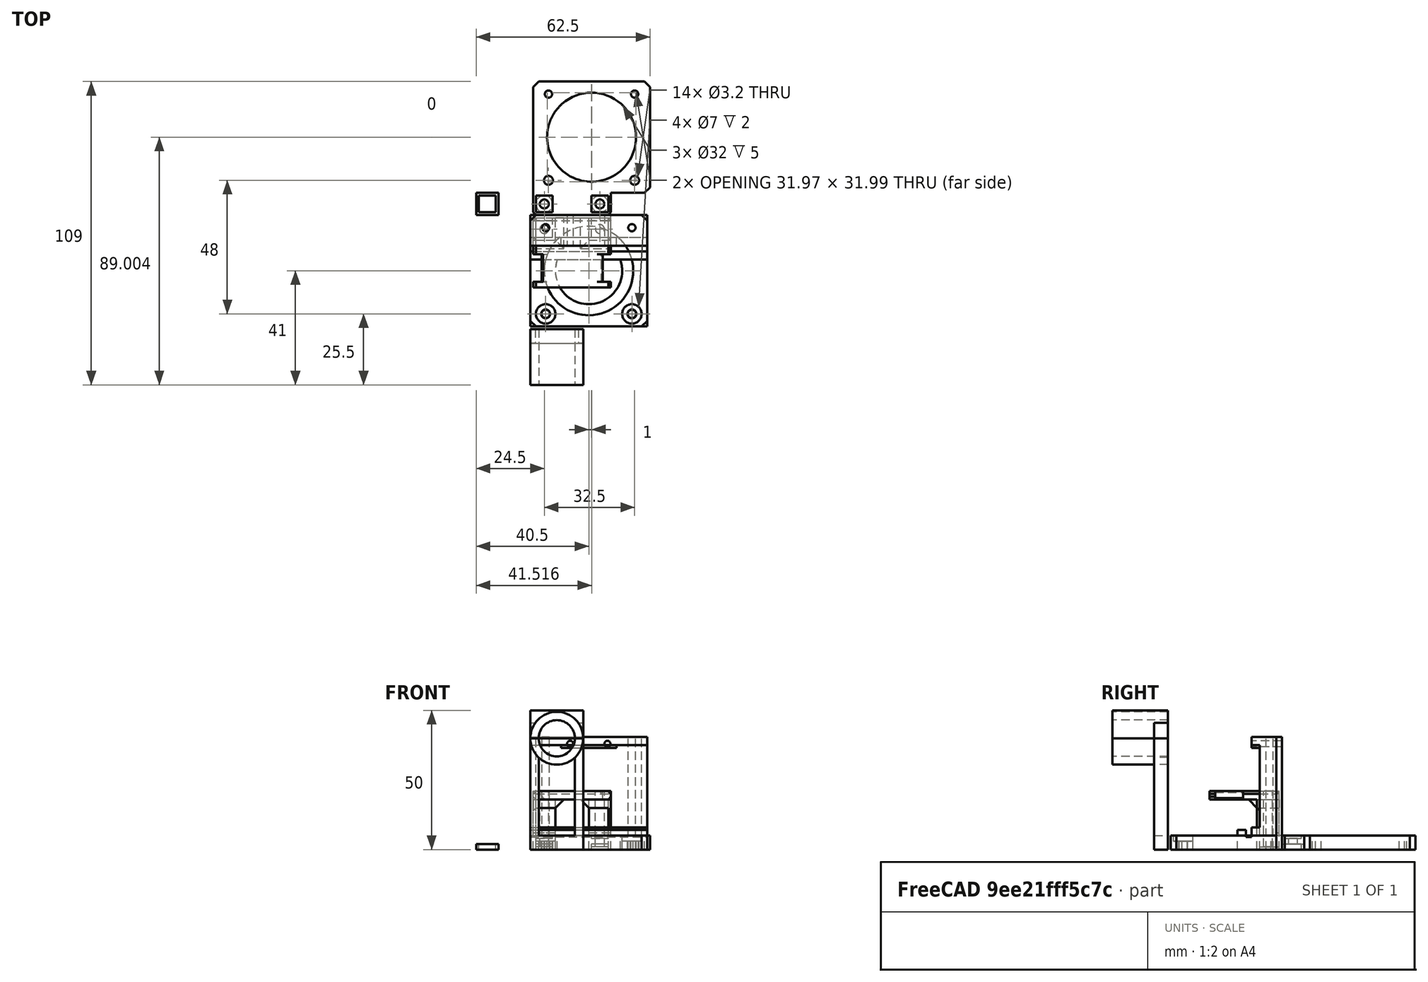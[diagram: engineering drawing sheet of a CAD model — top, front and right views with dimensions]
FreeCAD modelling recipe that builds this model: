
FCSTD DOCUMENT  (FreeCAD 0.18R14555 (Git shallow))
Label: extruder-wirebox-bottom
License: All rights reserved
LicenseURL: http://en.wikipedia.org/wiki/All_rights_reserved
objects: Part::Box×41, Part::Cylinder×25, Part::MultiFuse×21, Part::Cut×20, Part::Chamfer×9, Part::Feature×5, App::DocumentObjectGroup×1, Part::MultiCommon×1, Part::Fillet×1
note: 123 computed .brp shape members not serialized (recipe doc carries the construction recipe); baked Part::Feature solids carry a one-line shape summary decoded from their .brp

FEATURE [Part::Box] Box  label="Cube"
  AttacherType = Attacher::AttachEngine3D
  Height = 5
  Length = 42
  Placement = pos=(-1,-40,0) rot=(0,0,1;0rad)
  Width = 40
FEATURE [Part::Cylinder] Cylinder
  Angle = 360
  AttacherType = Attacher::AttachEngine3D
  Height = 50
  Placement = pos=(4.5,-4.5,0) rot=(0,0,1;0rad)
  Radius = 1.3
FEATURE [Part::Cylinder] Cylinder001
  Angle = 360
  AttacherType = Attacher::AttachEngine3D
  Height = 50
  Placement = pos=(35.5,-4.5,0) rot=(0,0,1;0rad)
  Radius = 1.3
FEATURE [Part::Box] Box001  label="Cube001"
  AttacherType = Attacher::AttachEngine3D
  Height = 40.5
  Length = 42
  Placement = pos=(-1,-8,0) rot=(0,0,1;0rad)
  Width = 8
FEATURE [Part::Box] Box002  label="Cube002"
  AttacherType = Attacher::AttachEngine3D
  Height = 8
  Length = 42
  Placement = pos=(-1,-11,0) rot=(0,0,1;0rad)
  Width = 3
FEATURE [Part::Box] Box003  label="Cube003"
  AttacherType = Attacher::AttachEngine3D
  Height = 7
  Length = 42
  Placement = pos=(-1,-16,0) rot=(0,0,1;0rad)
  Width = 3
FEATURE [Part::Cylinder] Cylinder006
  Angle = 360
  AttacherType = Attacher::AttachEngine3D
  Height = 5
  Placement = pos=(20,-20,0) rot=(0,0,1;0rad)
  Radius = 12
FEATURE [Part::Box] Box004  label="Cube004"
  AttacherType = Attacher::AttachEngine3D
  Height = 5
  Length = 42
  Placement = pos=(-1,-16,0) rot=(0,0,1;0rad)
  Width = 16
FEATURE [Part::Cut] Cut
  Base = -> Cylinder006
  Tool = -> Box004
FEATURE [Part::Box] Box005  label="Cube005"
  AttacherType = Attacher::AttachEngine3D
  Height = 5
  Length = 42
  Placement = pos=(-1,-11,35.5) rot=(0,0,1;0rad)
  Width = 3
FEATURE [Part::Cylinder] Cylinder007
  Angle = 360
  AttacherType = Attacher::AttachEngine3D
  Height = 11
  Placement = pos=(13.3,8e-15,38) rot=(1,0,0;1.5708rad)
  Radius = 1.1
FEATURE [Part::Cylinder] Cylinder008
  Angle = 360
  AttacherType = Attacher::AttachEngine3D
  Height = 11
  Placement = pos=(26.7,8e-15,38) rot=(1,0,0;1.5708rad)
  Radius = 1.1
FEATURE [App::DocumentObjectGroup] Group
FEATURE [Part::MultiFuse] Fusion
  Shapes = -> [Box005,Box001,Box003,Box002,Box]
FEATURE [Part::Box] Box006  label="Cube006"
  AttacherType = Attacher::AttachEngine3D
  Height = 2
  Length = 11
  Placement = pos=(-1,-11,35.5) rot=(0,0,1;0rad)
  Width = 3
FEATURE [Part::Box] Box007  label="Cube007"
  AttacherType = Attacher::AttachEngine3D
  Height = 2
  Length = 11
  Placement = pos=(30,-11,35.5) rot=(0,0,1;0rad)
  Width = 3
FEATURE [Part::Box] Box008  label="Cube008"
  AttacherType = Attacher::AttachEngine3D
  Height = 1
  Length = 20
  Placement = pos=(10,-11,35.5) rot=(0,0,1;0rad)
  Width = 3
FEATURE [Part::Box] Box009  label="Cube009"
  AttacherType = Attacher::AttachEngine3D
  Height = 2
  Length = 42
  Placement = pos=(-1,-13,4.5) rot=(0,0,1;0rad)
  Width = 2
FEATURE [Part::MultiFuse] Fusion002
  Shapes = -> [Box009,Box008,Box007,Box006]
FEATURE [Part::Cylinder] Cylinder009
  Angle = 360
  AttacherType = Attacher::AttachEngine3D
  Height = 2
  Placement = pos=(4.5,-35.5,3) rot=(0,0,1;0rad)
  Radius = 3.5
FEATURE [Part::Cylinder] Cylinder010
  Angle = 360
  AttacherType = Attacher::AttachEngine3D
  Height = 2
  Placement = pos=(35.5,-35.5,3) rot=(0,0,1;0rad)
  Radius = 3.5
FEATURE [Part::Cylinder] Cylinder011
  Angle = 360
  AttacherType = Attacher::AttachEngine3D
  Height = 5
  Placement = pos=(35.5,-35.5,0) rot=(0,0,1;0rad)
  Radius = 1.5
FEATURE [Part::Cylinder] Cylinder012
  Angle = 360
  AttacherType = Attacher::AttachEngine3D
  Height = 5
  Placement = pos=(4.5,-35.5,0) rot=(0,0,1;0rad)
  Radius = 1.5
FEATURE [Part::Cut] Cut001
  Base = -> Fusion
  Tool = -> Cut
FEATURE [Part::MultiFuse] Fusion003
  Shapes = -> [Cylinder,Cylinder001,Cylinder007,Cylinder008,Cylinder009,Cylinder010,Cylinder011,Cylinder012]
FEATURE [Part::Cut] Cut002
  Base = -> Cut001
  Tool = -> Fusion002
FEATURE [Part::Cut] Cut003
  Base = -> Cut002
  Tool = -> Fusion003
FEATURE [Part::Feature] Cut003001  label="Cut004"
  shape: bbox 42 x 40 x 40.5 mm, 31 faces (baked)
FEATURE [Part::Chamfer] Chamfer
  Base = -> Cut003001
  Edges = 4 edges r=2: [Edge27,Edge29,Edge47,Edge80]
FEATURE [Part::Feature] Chamfer_solid  label="Chamfer (Solid)"
  shape: bbox 42 x 40 x 40.5 mm, 35 faces (baked)
FEATURE [Part::Box] Box010  label="Cube010"
  AttacherType = Attacher::AttachEngine3D
  Height = 3
  Length = 11
  Placement = pos=(30,-11,37.5) rot=(0,0,1;0rad)
  Width = 3
FEATURE [Part::Box] Box011  label="Cube011"
  AttacherType = Attacher::AttachEngine3D
  Height = 3
  Length = 11
  Placement = pos=(-1,-11,37.5) rot=(0,0,1;0rad)
  Width = 3
FEATURE [Part::Box] Box012  label="Cube012"
  AttacherType = Attacher::AttachEngine3D
  Height = 1
  Length = 20
  Placement = pos=(10,-11,36.5) rot=(0,0,1;0rad)
  Width = 3
FEATURE [Part::Cylinder] Cylinder013
  Angle = 360
  AttacherType = Attacher::AttachEngine3D
  Height = 3
  Placement = pos=(4.5,-35.5,0) rot=(0,0,1;0rad)
  Radius = 1.6
FEATURE [Part::Cylinder] Cylinder014
  Angle = 360
  AttacherType = Attacher::AttachEngine3D
  Height = 3
  Placement = pos=(35.5,-35.5,0) rot=(0,0,1;0rad)
  Radius = 1.6
FEATURE [Part::Cylinder] Cylinder015
  Angle = 360
  AttacherType = Attacher::AttachEngine3D
  Height = 7
  Placement = pos=(20,-20,0) rot=(0,0,1;0rad)
  Radius = 12
FEATURE [Part::Box] Box013  label="Cube013"
  AttacherType = Attacher::AttachEngine3D
  Height = 10
  Length = 42
  Placement = pos=(-1,-13,0) rot=(0,0,1;0rad)
  Width = 12
FEATURE [Part::Cut] Cut003002
  Base = -> Cylinder015
  Tool = -> Box013
FEATURE [Part::Cut] Cut003003
  Base = -> Chamfer_solid
  Tool = -> Cut003002
FEATURE [Part::MultiFuse] Fusion004
  Shapes = -> [Cylinder013,Cylinder014]
FEATURE [Part::Cut] Cut003004
  Base = -> Cut003003
  Tool = -> Fusion004
FEATURE [Part::MultiFuse] Fusion005
  Shapes = -> [Box011,Box010]
FEATURE [Part::Cut] Cut003005
  Base = -> Cut003004
  Tool = -> Fusion005
FEATURE [Part::Box] Box014  label="Cube014"
  AttacherType = Attacher::AttachEngine3D
  Height = 15
  Length = 9
  Placement = pos=(-7,-8,25.5) rot=(0,0,1;0rad)
  Width = 8
FEATURE [Part::Box] Box015  label="Cube015"
  AttacherType = Attacher::AttachEngine3D
  Height = 15
  Length = 5
  Placement = pos=(-7,-48,25.5) rot=(0,0,1;0rad)
  Width = 48
FEATURE [Part::Box] Box016  label="Cube016"
  AttacherType = Attacher::AttachEngine3D
  Height = 2
  Length = 5
  Placement = pos=(-7,-46,25.5) rot=(0,0,1;0rad)
  Width = 3
FEATURE [Part::Box] Box017  label="Cube017"
  AttacherType = Attacher::AttachEngine3D
  Height = 2
  Length = 5
  Placement = pos=(-7,-40,25.5) rot=(0,0,1;0rad)
  Width = 3
FEATURE [Part::Box] Box018  label="Cube018"
  AttacherType = Attacher::AttachEngine3D
  Height = 2
  Length = 5
  Placement = pos=(-7,-46,38.5) rot=(0,0,1;0rad)
  Width = 3
FEATURE [Part::Box] Box019  label="Cube019"
  AttacherType = Attacher::AttachEngine3D
  Height = 2
  Length = 5
  Placement = pos=(-7,-40,38.5) rot=(0,0,1;0rad)
  Width = 3
FEATURE [Part::MultiFuse] Fusion006
  Shapes = -> [Box019,Box017,Box018,Box016]
FEATURE [Part::Cut] Cut003006
  Base = -> Box015
  Tool = -> Fusion006
FEATURE [Part::MultiFuse] Fusion007
  Shapes = -> [Cut003006,Box014,Cut003005]
FEATURE [Part::Box] Box020  label="Cube020"
  AttacherType = Attacher::AttachEngine3D
  Height = 10
  Length = 8
  Placement = pos=(-7,-8,16) rot=(0,0,1;0rad)
  Width = 8
FEATURE [Part::Chamfer] Chamfer001
  Base = -> Box020
  Edges = 1 edges r=6: [Edge4]
  Placement = pos=(0,0,3.5) rot=(0,0,1;0rad)
FEATURE [Part::MultiFuse] Fusion008
  Shapes = -> [Chamfer001,Fusion007]
FEATURE [Part::Box] Box021  label="Cube021"
  AttacherType = Attacher::AttachEngine3D
  Height = 2
  Length = 8
  Placement = pos=(-20.5,0,0) rot=(0,0,1;0rad)
  Width = 8
FEATURE [Part::Box] Box022  label="Cube022"
  AttacherType = Attacher::AttachEngine3D
  Height = 2
  Length = 6
  Placement = pos=(-19.5,1,0) rot=(0,0,1;0rad)
  Width = 6
FEATURE [Part::Cut] Cut003007
  Base = -> Box021
  Tool = -> Box022
FEATURE [Part::Box] Box023  label="Cube023"
  AttacherType = Attacher::AttachEngine3D
  Height = 5
  Length = 45
  Placement = pos=(-3,-46,0) rot=(0,0,1;0rad)
  Width = 46
FEATURE [Part::MultiCommon] Common
  Shapes = -> [Box023,Fusion008]
FEATURE [Part::Cylinder] Cylinder016
  Angle = 360
  AttacherType = Attacher::AttachEngine3D
  Height = 10
  Placement = pos=(20,-20,0) rot=(0,0,1;0rad)
  Radius = 16
FEATURE [Part::Box] Box024  label="Cube024"
  AttacherType = Attacher::AttachEngine3D
  Height = 5
  Length = 42
  Placement = pos=(-1,-19,0) rot=(0,0,1;0rad)
  Width = 11
FEATURE [Part::MultiFuse] Fusion009
  Shapes = -> [Common,Box024]
FEATURE [Part::Cut] Cut003008
  Base = -> Fusion009
  Tool = -> Cylinder016
FEATURE [Part::Cylinder] Cylinder017
  Angle = 360
  AttacherType = Attacher::AttachEngine3D
  Height = 10
  Placement = pos=(4.5,-35.5,0) rot=(0,0,1;0rad)
  Radius = 1.6
FEATURE [Part::Cylinder] Cylinder018
  Angle = 360
  AttacherType = Attacher::AttachEngine3D
  Height = 10
  Placement = pos=(35.5,-35.5,0) rot=(0,0,1;0rad)
  Radius = 1.6
FEATURE [Part::Cylinder] Cylinder019
  Angle = 360
  AttacherType = Attacher::AttachEngine3D
  Height = 5
  Placement = pos=(4.5,-35.5,0) rot=(0,0,1;0rad)
  Radius = 3.6
FEATURE [Part::Cylinder] Cylinder020
  Angle = 360
  AttacherType = Attacher::AttachEngine3D
  Height = 5
  Placement = pos=(35.5,-35.5,0) rot=(0,0,1;0rad)
  Radius = 3.6
FEATURE [Part::MultiFuse] Fusion010
  Shapes = -> [Cylinder020,Cylinder019,Cut003008]
FEATURE [Part::MultiFuse] Fusion011
  Shapes = -> [Cylinder018,Cylinder017]
FEATURE [Part::Cut] Cut003009
  Base = -> Fusion010
  Tool = -> Fusion011
FEATURE [Part::Feature] Cut003009001  label="Cut003010"
  shape: bbox 42 x 40 x 5 mm, 15 faces (baked)
FEATURE [Part::Box] Box025  label="Cube025"
  AttacherType = Attacher::AttachEngine3D
  Height = 45.5
  Length = 19
  Placement = pos=(-1,-46,0) rot=(0,0,1;0rad)
  Width = 5
FEATURE [Part::Box] Box026  label="Cube026"
  AttacherType = Attacher::AttachEngine3D
  Height = 45.5
  Length = 13
  Placement = pos=(2,-46,5) rot=(0,0,1;0rad)
  Width = 5
FEATURE [Part::Cut] Cut003009002
  Base = -> Box025
  Tool = -> Box026
FEATURE [Part::Cylinder] Cylinder021
  Angle = 360
  AttacherType = Attacher::AttachEngine3D
  Height = 20
  Placement = pos=(8.5,-41,40) rot=(1,0,0;1.5708rad)
  Radius = 9.5
FEATURE [Part::Cylinder] Cylinder022
  Angle = 360
  AttacherType = Attacher::AttachEngine3D
  Height = 20
  Placement = pos=(8.5,-41,40) rot=(1,0,0;1.5708rad)
  Radius = 6.5
FEATURE [Part::Cut] Cut003009003
  Base = -> Cylinder021
  Tool = -> Cylinder022
FEATURE [Part::Box] Box027  label="Cube027"
  AttacherType = Attacher::AttachEngine3D
  Height = 5
  Length = 28
  Placement = pos=(-1,-48,0) rot=(0,0,1;0rad)
  Width = 10
FEATURE [Part::Box] Box028  label="Cube028"
  AttacherType = Attacher::AttachEngine3D
  Height = 10
  Length = 19
  Placement = pos=(-1,-61,40) rot=(0,0,1;0rad)
  Width = 20
FEATURE [Part::MultiFuse] Fusion012
  Shapes = -> [Cut003009003,Cut003009002]
FEATURE [Part::Cylinder] Cylinder023
  Angle = 360
  AttacherType = Attacher::AttachEngine3D
  Height = 2
  Placement = pos=(23,-44,0) rot=(0,0,1;0rad)
  Radius = 3
FEATURE [Part::Cylinder] Cylinder024
  Angle = 360
  AttacherType = Attacher::AttachEngine3D
  Height = 2
  Placement = pos=(3,-44,0) rot=(0,0,1;0rad)
  Radius = 3
FEATURE [Part::Cylinder] Cylinder025
  Angle = 360
  AttacherType = Attacher::AttachEngine3D
  Height = 5
  Placement = pos=(3,-44,0) rot=(0,0,1;0rad)
  Radius = 1.6
FEATURE [Part::Cylinder] Cylinder026
  Angle = 360
  AttacherType = Attacher::AttachEngine3D
  Height = 5
  Placement = pos=(23,-44,0) rot=(0,0,1;0rad)
  Radius = 1.6
FEATURE [Part::MultiFuse] Fusion013
  Shapes = -> [Cylinder026,Cylinder025]
FEATURE [Part::Cut] Cut003009004
  Base = -> Box027
  Tool = -> Fusion013
FEATURE [Part::MultiFuse] Fusion014
  Shapes = -> [Cylinder024,Cylinder023]
FEATURE [Part::Cut] Cut003009005
  Base = -> Cut003009004
  Tool = -> Fusion014
FEATURE [Part::Box] Box029  label="Cube029"
  AttacherType = Attacher::AttachEngine3D
  Height = 1
  Length = 6
  Placement = pos=(0,-47,4) rot=(0,0,1;0rad)
  Width = 6
FEATURE [Part::Box] Box030  label="Cube030"
  AttacherType = Attacher::AttachEngine3D
  Height = 1
  Length = 6
  Placement = pos=(20,-47,4) rot=(0,0,1;0rad)
  Width = 6
FEATURE [Part::MultiFuse] Fusion015
  Shapes = -> [Box030,Box029]
FEATURE [Part::Cut] Cut003009006
  Base = -> Cut003009005
  Tool = -> Fusion015
FEATURE [Part::Chamfer] Chamfer002
  Base = -> Cut003009006
  Edges = 2 edges r=1: [Edge1,Edge6]
FEATURE [Part::MultiFuse] Fusion016
  Placement = pos=(1,48,0) rot=(0,0,1;0rad)
  Shapes = -> [Chamfer002,Cut003009001]
FEATURE [Part::Box] Box031  label="Cube031"
  AttacherType = Attacher::AttachEngine3D
  Height = 1
  Length = 6
  Placement = pos=(1,-8,0) rot=(0,0,1;0rad)
  Width = 7
FEATURE [Part::Box] Box032  label="Cube032"
  AttacherType = Attacher::AttachEngine3D
  Height = 1
  Length = 6
  Placement = pos=(21,-8,0) rot=(0,0,1;0rad)
  Width = 7
FEATURE [Part::Cylinder] Cylinder027
  Angle = 360
  AttacherType = Attacher::AttachEngine3D
  Height = 21
  Placement = pos=(4,-5,0) rot=(0,0,1;0rad)
  Radius = 1.6
FEATURE [Part::Cylinder] Cylinder028
  Angle = 360
  AttacherType = Attacher::AttachEngine3D
  Height = 21
  Placement = pos=(24,-5,0) rot=(0,0,1;0rad)
  Radius = 1.6
FEATURE [Part::Box] Box033  label="Cube033"
  AttacherType = Attacher::AttachEngine3D
  Height = 21
  Length = 8
  Placement = pos=(0,-9,0) rot=(0,0,1;0rad)
  Width = 8
FEATURE [Part::Box] Box034  label="Cube034"
  AttacherType = Attacher::AttachEngine3D
  Height = 21
  Length = 8
  Placement = pos=(20,-9,0) rot=(0,0,1;0rad)
  Width = 8
FEATURE [Part::MultiFuse] Fusion017
  Shapes = -> [Box032,Cylinder028,Box031,Cylinder027]
FEATURE [Part::MultiFuse] Fusion018
  Shapes = -> [Box033,Box034]
FEATURE [Part::Cut] Cut003009007
  Base = -> Fusion018
  Tool = -> Fusion017
FEATURE [Part::Box] Box035  label="Cube035"
  AttacherType = Attacher::AttachEngine3D
  Height = 3
  Length = 28
  Placement = pos=(0,-26,18) rot=(0,0,1;0rad)
  Width = 17
FEATURE [Part::Box] Box036  label="Cube036"
  AttacherType = Attacher::AttachEngine3D
  Height = 3
  Length = 3
  Placement = pos=(0,-24,18) rot=(0,0,1;0rad)
  Width = 10
FEATURE [Part::Box] Box037  label="Cube037"
  AttacherType = Attacher::AttachEngine3D
  Height = 3
  Length = 3
  Placement = pos=(25,-24,18) rot=(0,0,1;0rad)
  Width = 10
FEATURE [Part::Box] Box038  label="Cube038"
  AttacherType = Attacher::AttachEngine3D
  Height = 3
  Length = 12
  Placement = pos=(8,-9,18) rot=(0,0,1;0rad)
  Width = 8
FEATURE [Part::MultiFuse] Fusion019
  Shapes = -> [Box035,Cut003009007,Box038]
FEATURE [Part::MultiFuse] Fusion020
  Shapes = -> [Box037,Box036]
FEATURE [Part::Cut] Cut003009008
  Base = -> Fusion019
  Tool = -> Fusion020
FEATURE [Part::Feature] Cut003009008001  label="Cut003009009"
  shape: bbox 28 x 25 x 21 mm, 30 faces (baked)
FEATURE [Part::Fillet] Fillet
  Base = -> Cut003009008001
  Edges = 2 edges r=2: [Edge34,Edge53]
FEATURE [Part::Chamfer] Chamfer003
  Base = -> Fillet
  Edges = 1 edges r=0.5: [Edge9]
FEATURE [Part::Chamfer] Chamfer004
  Base = -> Chamfer003
  Edges = 4 edges r=1: [Edge18,Edge20,Edge35,Edge37]
FEATURE [Part::Chamfer] Chamfer005
  Base = -> Chamfer004
  Edges = 1 edges r=0.5: [Edge88]
FEATURE [Part::Chamfer] Chamfer006
  Base = -> Chamfer005
  Edges = 5 edges r=1: [Edge23,Edge25,Edge27,Edge61,Edge70]
FEATURE [Part::Chamfer] Chamfer007
  Base = -> Chamfer006
  Edges = 4 edges r=3: [Edge80,Edge81,Edge83,Edge84]
FEATURE [Part::Feature] Fusion016001  label="Fusion021"
  shape: bbox 42 x 48 x 5 mm, 34 faces (baked)
FEATURE [Part::Box] Box039  label="Cube039"
  AttacherType = Attacher::AttachEngine3D
  Height = 6
  Length = 8
  Placement = pos=(0,-2,0) rot=(0,0,1;0rad)
  Width = 1
FEATURE [Part::Box] Box040  label="Cube040"
  AttacherType = Attacher::AttachEngine3D
  Height = 6
  Length = 8
  Placement = pos=(20,-2,0) rot=(0,0,1;0rad)
  Width = 1
FEATURE [Part::MultiFuse] Fusion016002
  Shapes = -> [Box039,Box040]
FEATURE [Part::Cut] Cut003009008002
  Base = -> Chamfer007
  Tool = -> Fusion016002
FEATURE [Part::Chamfer] Chamfer008
  Base = -> Cut003009008002
  Edges = 2 edges r=1: [Edge1,Edge65]
